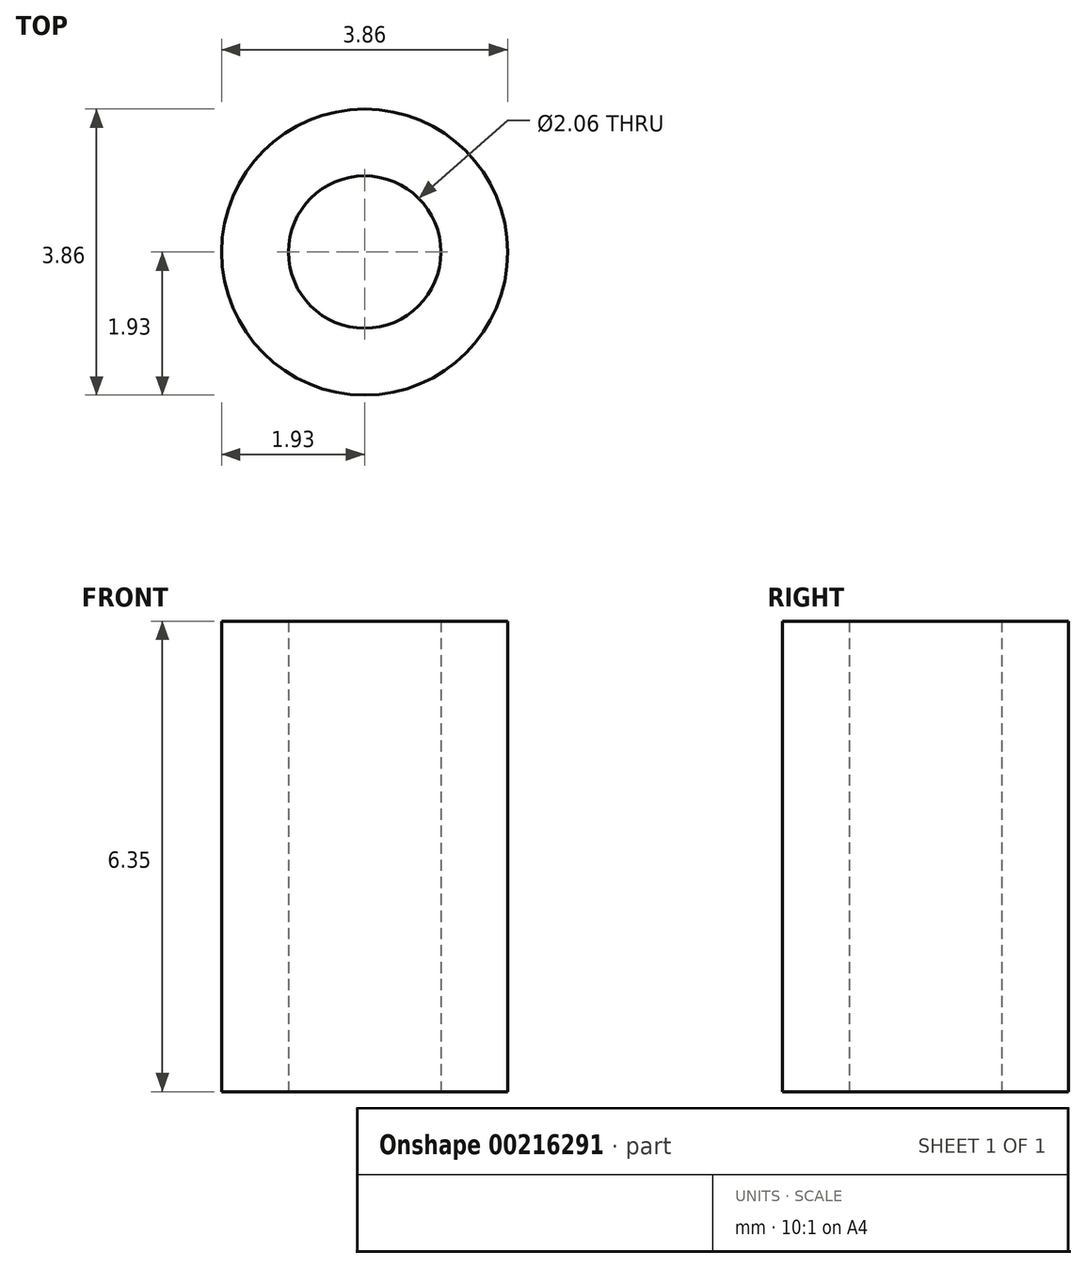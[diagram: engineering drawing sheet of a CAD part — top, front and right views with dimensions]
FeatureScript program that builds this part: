
annotation { "Feature Type Name" : "Feature", "Feature Type Description" : "" }
export const myFeature = defineFeature(function(context is Context, id is Id, definition is map)
    precondition{}
    {
        {
            var Q0;
            Q0=qCreatedBy(makeId("Top.planeOp"),FACE);
            var sketch = newSketch(context, id + "F0", { "sketchPlane" : qUnion([Q0])});
            skCircle(sketch, "E0", {"center": v(0, 0) * mm, "radius": 1.03 * mm});
            skCircle(sketch, "E1", {"center": v(0, 0) * mm, "radius": 1.93 * mm});
            skSolve(sketch);
        }
        {
            var Q0;
            Q0 = qSketchRegion(id + "F0", true);
            extrude(context, id + "F1", {"entities" : qUnion([Q0]), "depth" : 6.35 * mm});
        }
    });
